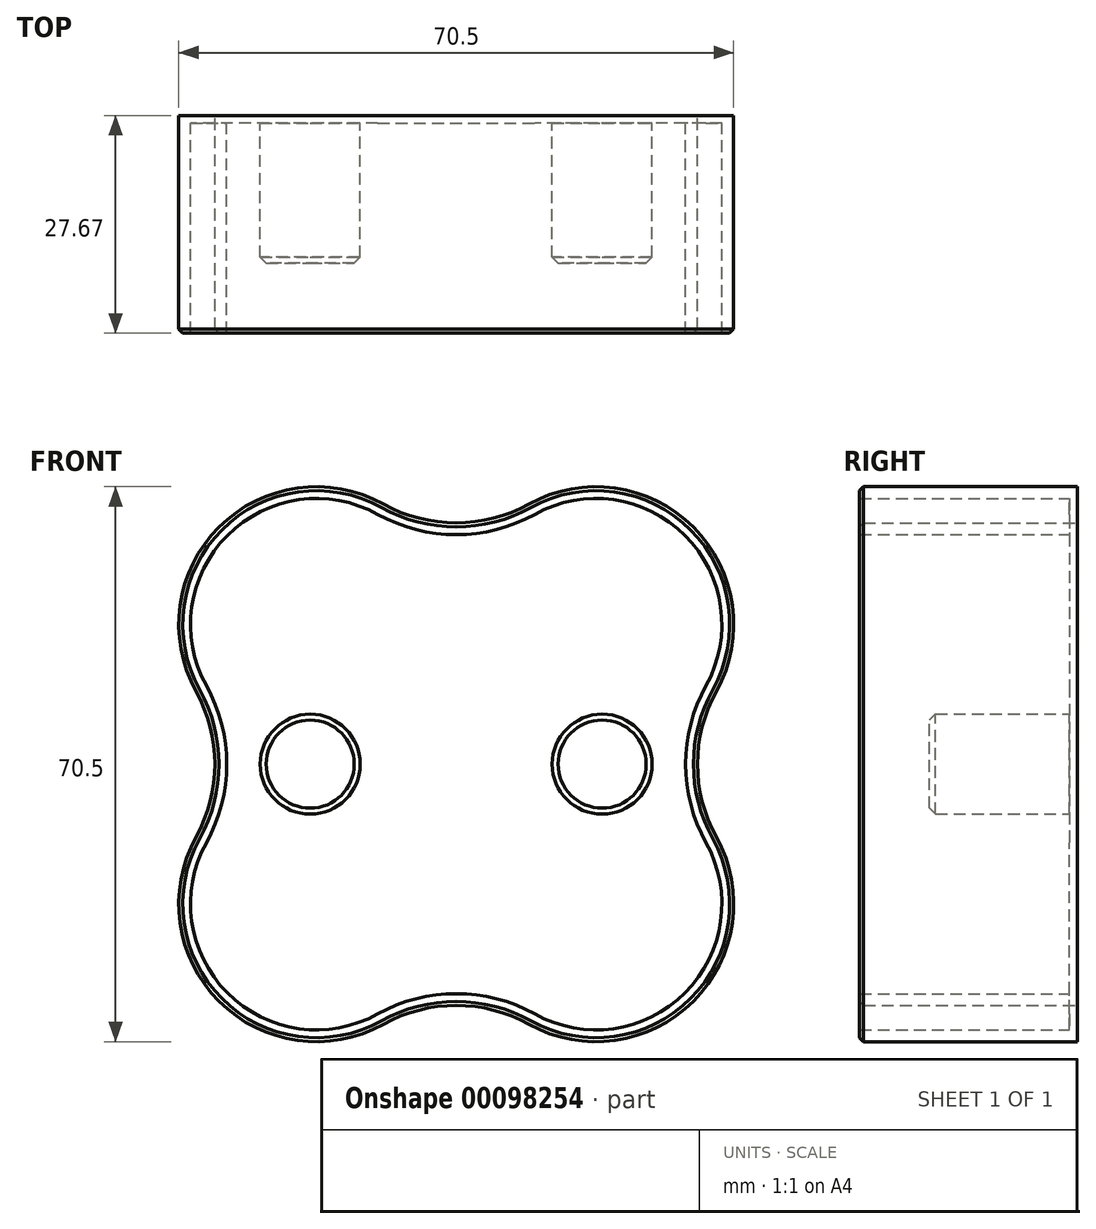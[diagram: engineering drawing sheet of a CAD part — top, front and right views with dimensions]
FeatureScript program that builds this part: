
annotation { "Feature Type Name" : "Feature", "Feature Type Description" : "" }
export const myFeature = defineFeature(function(context is Context, id is Id, definition is map)
    precondition{}
    {
        {
            var Q0;
            Q0=qCreatedBy(makeId("Front.planeOp"),FACE);
            var sketch = newSketch(context, id + "F0", { "sketchPlane" : qUnion([Q0])});
            skLineSegment(sketch, "E0.bottom", {"start": v(17.75, 17.75) * mm, "end": v(-17.75, 17.75) * mm, "construction": true});
            skLineSegment(sketch, "E0.top", {"start": v(17.75, -17.75) * mm, "end": v(-17.75, -17.75) * mm, "construction": true});
            skLineSegment(sketch, "E0.left", {"start": v(17.75, 17.75) * mm, "end": v(17.75, -17.75) * mm, "construction": true});
            skLineSegment(sketch, "E0.right", {"start": v(-17.75, 17.75) * mm, "end": v(-17.75, -17.75) * mm, "construction": true});
            skPoint(sketch, "E0.middle", {"position": v(0, 0) * mm});
            skArc(sketch, "E1", {"start": v(-33.05, 9.25) * mm, "mid": v(-30.12, 30.12) * mm, "end": v(-9.25, 33.05) * mm});
            skArc(sketch, "E2", {"start": v(9.25, 33.05) * mm, "mid": v(30.12, 30.12) * mm, "end": v(33.05, 9.25) * mm});
            skArc(sketch, "E3", {"start": v(33.05, -9.25) * mm, "mid": v(30.12, -30.12) * mm, "end": v(9.25, -33.05) * mm});
            skArc(sketch, "E4", {"start": v(-33.05, -9.25) * mm, "mid": v(-30.12, -30.12) * mm, "end": v(-9.25, -33.05) * mm});
            skArc(sketch, "E5", {"start": v(-33.05, 9.25) * mm, "mid": v(-30.65, 0) * mm, "end": v(-33.05, -9.25) * mm});
            skArc(sketch, "E6", {"start": v(-9.25, -33.05) * mm, "mid": v(0, -30.65) * mm, "end": v(9.25, -33.05) * mm});
            skArc(sketch, "E7", {"start": v(33.05, -9.25) * mm, "mid": v(30.65, 0) * mm, "end": v(33.05, 9.25) * mm});
            skArc(sketch, "E8", {"start": v(-9.25, 33.05) * mm, "mid": v(0, 30.65) * mm, "end": v(9.25, 33.05) * mm});
            skSolve(sketch);
        }
        {
            var Q0;
            Q0 = qSketchRegion(id + "F0", true);
            extrude(context, id + "F1", {"entities" : qUnion([Q0]), "depth" : 1 * mm});
        }
        {
            var Q0;
            Q0=makeQuery(id+"F1.opExtrude","CAP_FACE",FACE,{"disambiguationData":[OSD([sQuery(id+"F0.wireOp",EDGE,"E1"),sQuery(id+"F0.wireOp",EDGE,"E2"),sQuery(id+"F0.wireOp",EDGE,"E3"),sQuery(id+"F0.wireOp",EDGE,"E4"),sQuery(id+"F0.wireOp",EDGE,"E5"),sQuery(id+"F0.wireOp",EDGE,"E6"),sQuery(id+"F0.wireOp",EDGE,"E7"),sQuery(id+"F0.wireOp",EDGE,"E8")])],"isStart":false});
            var sketch = newSketch(context, id + "F2", { "sketchPlane" : qUnion([Q0])});
            skArc(sketch, "E9", {"start": v(-33.05, 9.25) * mm, "mid": v(-30.12, 30.12) * mm, "end": v(-9.25, 33.05) * mm});
            skArc(sketch, "E10", {"start": v(9.25, 33.05) * mm, "mid": v(30.12, 30.12) * mm, "end": v(33.05, 9.25) * mm});
            skArc(sketch, "E11", {"start": v(33.05, -9.25) * mm, "mid": v(30.12, -30.12) * mm, "end": v(9.25, -33.05) * mm});
            skArc(sketch, "E12", {"start": v(-33.05, -9.25) * mm, "mid": v(-30.12, -30.12) * mm, "end": v(-9.25, -33.05) * mm});
            skArc(sketch, "E13", {"start": v(-33.05, 9.25) * mm, "mid": v(-30.65, 0) * mm, "end": v(-33.05, -9.25) * mm});
            skArc(sketch, "E14", {"start": v(-9.25, 33.05) * mm, "mid": v(0, 30.65) * mm, "end": v(9.25, 33.05) * mm});
            skArc(sketch, "E15", {"start": v(33.05, 9.25) * mm, "mid": v(30.65, 0) * mm, "end": v(33.05, -9.25) * mm});
            skArc(sketch, "E16", {"start": v(-9.25, -33.05) * mm, "mid": v(0, -30.65) * mm, "end": v(9.25, -33.05) * mm});
            skArc(sketch, "E17.0", {"start": v(9.98, 31.74) * mm, "mid": v(0, 29.15) * mm, "end": v(-9.98, 31.74) * mm});
            skArc(sketch, "E17.1", {"start": v(31.74, 9.98) * mm, "mid": v(29.06, 29.06) * mm, "end": v(9.98, 31.74) * mm});
            skArc(sketch, "E17.2", {"start": v(-9.98, 31.74) * mm, "mid": v(-29.06, 29.06) * mm, "end": v(-31.74, 9.98) * mm});
            skArc(sketch, "E17.3", {"start": v(31.74, -9.98) * mm, "mid": v(29.15, 0) * mm, "end": v(31.74, 9.98) * mm});
            skArc(sketch, "E17.4", {"start": v(-31.74, 9.98) * mm, "mid": v(-29.15, 0) * mm, "end": v(-31.74, -9.98) * mm});
            skArc(sketch, "E17.5", {"start": v(-31.74, -9.98) * mm, "mid": v(-29.06, -29.06) * mm, "end": v(-9.98, -31.74) * mm});
            skArc(sketch, "E17.6", {"start": v(-9.98, -31.74) * mm, "mid": v(0, -29.15) * mm, "end": v(9.98, -31.74) * mm});
            skArc(sketch, "E17.7", {"start": v(9.98, -31.74) * mm, "mid": v(29.06, -29.06) * mm, "end": v(31.74, -9.98) * mm});
            skSolve(sketch);
        }
        {
            var Q0;
            Q0 = qSketchRegion(id + "F2", true);
            extrude(context, id + "F3", {"entities" : qUnion([Q0]), "operationType" : NewBodyOperationType.ADD, "depth" : 26.67 * mm});
        }
        {
            var Q0;
            Q0=makeQuery(id+"F1.opExtrude","CAP_FACE",FACE,{"disambiguationData":[OSD([sQuery(id+"F0.wireOp",EDGE,"E1"),sQuery(id+"F0.wireOp",EDGE,"E2"),sQuery(id+"F0.wireOp",EDGE,"E3"),sQuery(id+"F0.wireOp",EDGE,"E4"),sQuery(id+"F0.wireOp",EDGE,"E5"),sQuery(id+"F0.wireOp",EDGE,"E6"),sQuery(id+"F0.wireOp",EDGE,"E7"),sQuery(id+"F0.wireOp",EDGE,"E8")])],"isStart":false});
            var sketch = newSketch(context, id + "F4", { "sketchPlane" : qUnion([Q0])});
            skLineSegment(sketch, "E18", {"start": v(-18.54, 0) * mm, "end": v(18.54, 0) * mm, "construction": true});
            skCircle(sketch, "E19", {"center": v(-18.54, 0) * mm, "radius": 6.35 * mm});
            skCircle(sketch, "E20", {"center": v(18.54, 0) * mm, "radius": 6.35 * mm});
            skPoint(sketch, "E21", {"position": v(-12.2, 0) * mm});
            skPoint(sketch, "E22", {"position": v(12.2, 0) * mm});
            skSolve(sketch);
        }
        {
            var Q0;
            Q0 = qSketchRegion(id + "F4", true);
            extrude(context, id + "F5", {"entities" : qUnion([Q0]), "operationType" : NewBodyOperationType.ADD, "depth" : 17.78 * mm});
        }
        {
            var Q0;
            Q0=makeQuery(id+"F5.opExtrude","CAP_EDGE",EDGE,{"disambiguationData":[OSD([sQuery(id+"F4.wireOp",EDGE,"E20")])],"isStart":false});
            var Q1;
            Q1=makeQuery(id+"F5.opExtrude","CAP_EDGE",EDGE,{"disambiguationData":[OSD([sQuery(id+"F4.wireOp",EDGE,"E19")])],"isStart":false});
            chamfer(context, id + "F6", {"entities" : qUnion([Q0, Q1]), "width" : 0.76 * mm, "tangentPropagation" : true});
        }
        {
            var Q0;
            Q0=makeQuery(id+"F3.opExtrude","CAP_EDGE",EDGE,{"disambiguationData":[OSD([sQuery(id+"F2.wireOp",EDGE,"E9")])],"isStart":false});
            chamfer(context, id + "F7", {"entities" : qUnion([Q0]), "width" : 0.5 * mm, "tangentPropagation" : true});
        }
    });
